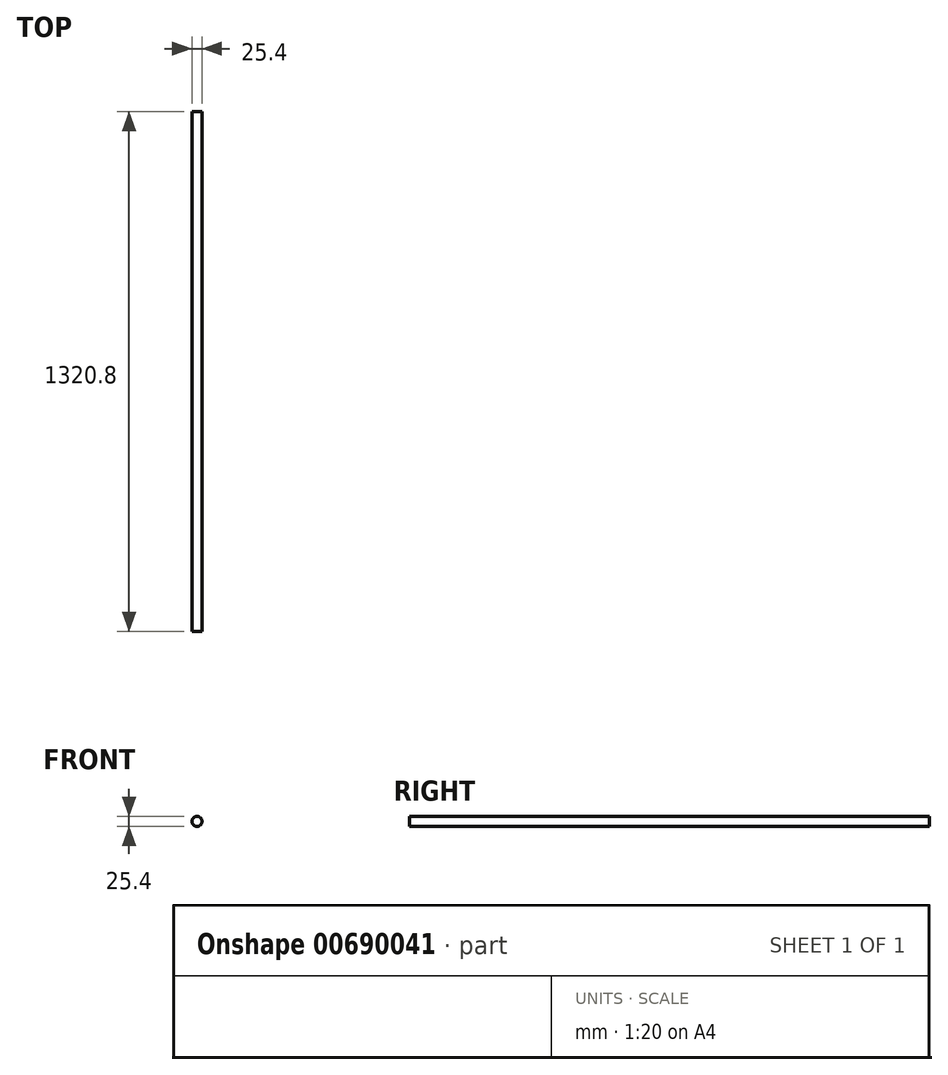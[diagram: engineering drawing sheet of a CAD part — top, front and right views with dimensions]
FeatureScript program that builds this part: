
annotation { "Feature Type Name" : "Feature", "Feature Type Description" : "" }
export const myFeature = defineFeature(function(context is Context, id is Id, definition is map)
    precondition{}
    {
        {
            var Q0;
            Q0=qCreatedBy(makeId("Front.planeOp"),FACE);
            var sketch = newSketch(context, id + "F0", { "sketchPlane" : qUnion([Q0])});
            skCircle(sketch, "E0", {"center": v(0, 0) * mm, "radius": 12.7 * mm});
            skSolve(sketch);
        }
        {
            var Q0;
            Q0 = qSketchRegion(id + "F0", true);
            extrude(context, id + "F1", {"entities" : qUnion([Q0]), "depth" : 1320.8 * mm, "offsetDistance" : 25.4 * mm});
        }
    });
